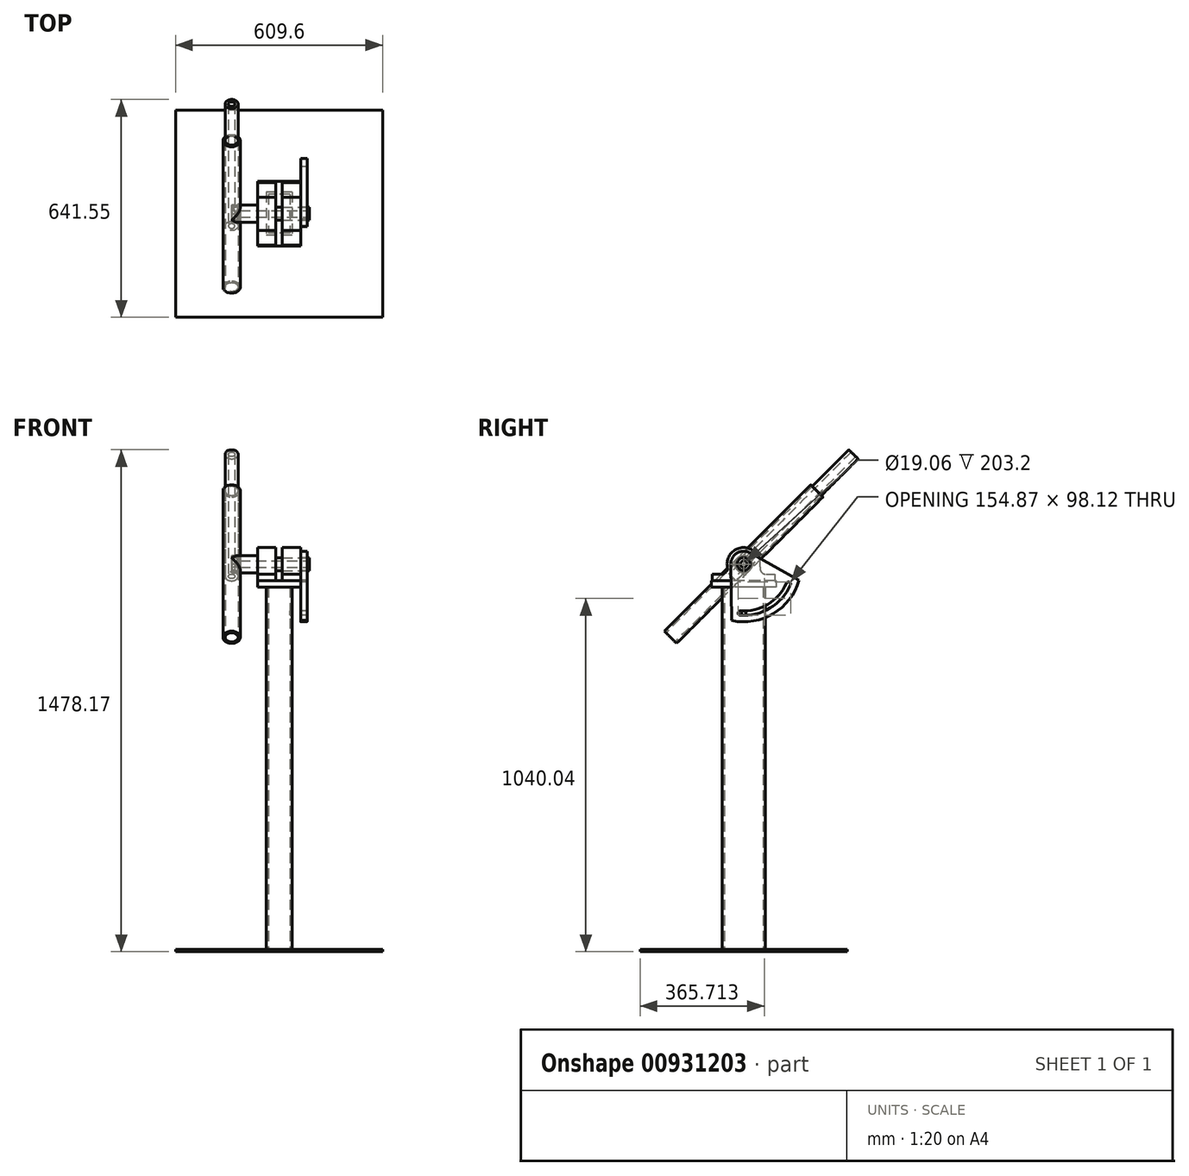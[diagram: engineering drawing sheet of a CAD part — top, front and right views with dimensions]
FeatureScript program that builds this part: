
annotation { "Feature Type Name" : "Feature", "Feature Type Description" : "" }
export const myFeature = defineFeature(function(context is Context, id is Id, definition is map)
    precondition{}
    {
        {
            var Q0;
            Q0=qCreatedBy(makeId("Top.planeOp"),FACE);
            var sketch = newSketch(context, id + "F0", { "sketchPlane" : qUnion([Q0])});
            skLineSegment(sketch, "E0.bottom", {"start": v(304.8, 304.8) * mm, "end": v(-304.8, 304.8) * mm});
            skLineSegment(sketch, "E0.top", {"start": v(304.8, -304.8) * mm, "end": v(-304.8, -304.8) * mm});
            skLineSegment(sketch, "E0.left", {"start": v(304.8, 304.8) * mm, "end": v(304.8, -304.8) * mm});
            skLineSegment(sketch, "E0.right", {"start": v(-304.8, 304.8) * mm, "end": v(-304.8, -304.8) * mm});
            skPoint(sketch, "E0.middle", {"position": v(0, 0) * mm});
            skSolve(sketch);
        }
        {
            var Q0;
            Q0 = qSketchRegion(id + "F0", true);
            extrude(context, id + "F1", {"entities" : qUnion([Q0]), "depth" : 6.35 * mm, "offsetDistance" : 25.4 * mm});
        }
        {
            var Q0;
            Q0=makeQuery(id+"F1.opExtrude","CAP_FACE",FACE,{"disambiguationData":[OSD([sQuery(id+"F0.wireOp",EDGE,"E0.bottom"),sQuery(id+"F0.wireOp",EDGE,"E0.top"),sQuery(id+"F0.wireOp",EDGE,"E0.left"),sQuery(id+"F0.wireOp",EDGE,"E0.right")])],"isStart":false});
            var sketch = newSketch(context, id + "F2", { "sketchPlane" : qUnion([Q0])});
            skLineSegment(sketch, "E1.bottom", {"start": v(38.1, 63.5) * mm, "end": v(-38.1, 63.5) * mm});
            skLineSegment(sketch, "E1.top", {"start": v(38.1, -63.5) * mm, "end": v(-38.1, -63.5) * mm});
            skLineSegment(sketch, "E1.left", {"start": v(38.1, 63.5) * mm, "end": v(38.1, -63.5) * mm});
            skLineSegment(sketch, "E1.right", {"start": v(-38.1, 63.5) * mm, "end": v(-38.1, -63.5) * mm});
            skPoint(sketch, "E1.middle", {"position": v(0, 0) * mm});
            skLineSegment(sketch, "E2.bottom", {"start": v(31.75, 57.15) * mm, "end": v(-31.75, 57.15) * mm});
            skLineSegment(sketch, "E2.top", {"start": v(31.75, -57.15) * mm, "end": v(-31.75, -57.15) * mm});
            skLineSegment(sketch, "E2.left", {"start": v(31.75, 57.15) * mm, "end": v(31.75, -57.15) * mm});
            skLineSegment(sketch, "E2.right", {"start": v(-31.75, 57.15) * mm, "end": v(-31.75, -57.15) * mm});
            skSolve(sketch);
        }
        {
            var Q0;
            Q0 = qSketchRegion(id + "F2", true);
            extrude(context, id + "F3", {"entities" : qUnion([Q0]), "depth" : 1066.8 * mm, "offsetDistance" : 25.4 * mm});
        }
        {
            var Q0;
            Q0=makeQuery(id+"F3.opExtrude","CAP_FACE",FACE,{"disambiguationData":[OSD([sQuery(id+"F2.wireOp",EDGE,"E1.bottom"),sQuery(id+"F2.wireOp",EDGE,"E1.top"),sQuery(id+"F2.wireOp",EDGE,"E1.left"),sQuery(id+"F2.wireOp",EDGE,"E1.right"),sQuery(id+"F2.wireOp",EDGE,"E2.bottom"),sQuery(id+"F2.wireOp",EDGE,"E2.top"),sQuery(id+"F2.wireOp",EDGE,"E2.left"),sQuery(id+"F2.wireOp",EDGE,"E2.right")])],"isStart":false});
            var sketch = newSketch(context, id + "F4", { "sketchPlane" : qUnion([Q0])});
            skLineSegment(sketch, "E3", {"start": v(-38.1, -63.5) * mm, "end": v(38.1, 63.5) * mm, "construction": true});
            skLineSegment(sketch, "E4.bottom", {"start": v(-63.5, 95.25) * mm, "end": v(63.5, 95.25) * mm});
            skLineSegment(sketch, "E4.top", {"start": v(-63.5, -95.25) * mm, "end": v(63.5, -95.25) * mm});
            skLineSegment(sketch, "E4.left", {"start": v(-63.5, 95.25) * mm, "end": v(-63.5, -95.25) * mm});
            skLineSegment(sketch, "E4.right", {"start": v(63.5, 95.25) * mm, "end": v(63.5, -95.25) * mm});
            skPoint(sketch, "E4.middle", {"position": v(0, 0) * mm});
            skSolve(sketch);
        }
        {
            var Q0;
            Q0 = qSketchRegion(id + "F4", true);
            extrude(context, id + "F5", {"entities" : qUnion([Q0]), "depth" : 19.05 * mm, "offsetDistance" : 25.4 * mm});
        }
        {
            var Q0;
            Q0=makeQuery(id+"F5.opExtrude","SWEPT_FACE",FACE,{"disambiguationData":[OSD([sQuery(id+"F4.wireOp",EDGE,"E4.left")])]});
            var sketch = newSketch(context, id + "F6", { "sketchPlane" : qUnion([Q0])});
            skCircle(sketch, "E5", {"center": v(0, 1141.4) * mm, "radius": 19.05 * mm});
            skArc(sketch, "E6", {"start": v(48.1, 1133.18) * mm, "mid": v(0, 1190.2) * mm, "end": v(-48.1, 1133.18) * mm});
            skLineSegment(sketch, "E7.bottom", {"start": v(92, 1111.25) * mm, "end": v(66.6, 1111.25) * mm});
            skLineSegment(sketch, "E7.top", {"start": v(92, 1092.2) * mm, "end": v(-92, 1092.2) * mm});
            skLineSegment(sketch, "E7.left", {"start": v(92, 1111.25) * mm, "end": v(92, 1092.2) * mm});
            skLineSegment(sketch, "E7.right", {"start": v(-92, 1111.25) * mm, "end": v(-92, 1092.2) * mm});
            skLineSegment(sketch, "E8", {"start": v(0, 1141.4) * mm, "end": v(0, 1092.2) * mm, "construction": true});
            skArc(sketch, "E9", {"start": v(48.1, 1133.18) * mm, "mid": v(52.26, 1117.92) * mm, "end": v(66.6, 1111.25) * mm});
            skArc(sketch, "E10", {"start": v(-66.6, 1111.25) * mm, "mid": v(-52.26, 1117.92) * mm, "end": v(-48.1, 1133.18) * mm});
            skPoint(sketch, "E11.0", {"position": v(0, 1092.2) * mm});
            skLineSegment(sketch, "E12.trimOffspring", {"start": v(-66.6, 1111.25) * mm, "end": v(-92, 1111.25) * mm});
            skSolve(sketch);
        }
        {
            var Q0;
            Q0 = qSketchRegion(id + "F6", true);
            extrude(context, id + "F7", {"entities" : qUnion([Q0]), "oppositeDirection" : true, "depth" : 54 * mm, "offsetDistance" : 25.4 * mm});
        }
        {
            var Q0;
            Q0=makeQuery(id+"F5.opExtrude","SWEPT_FACE",FACE,{"disambiguationData":[OSD([sQuery(id+"F4.wireOp",EDGE,"E4.right")])]});
            var sketch = newSketch(context, id + "F8", { "sketchPlane" : qUnion([Q0])});
            skLineSegment(sketch, "E13.0", {"start": v(-92, 1111.25) * mm, "end": v(-92, 1092.2) * mm});
            skLineSegment(sketch, "E14.0", {"start": v(-92, 1111.25) * mm, "end": v(-66.6, 1111.25) * mm});
            skLineSegment(sketch, "E15.0", {"start": v(-92, 1092.2) * mm, "end": v(92, 1092.2) * mm});
            skArc(sketch, "E16.0", {"start": v(-48.1, 1133.18) * mm, "mid": v(-52.26, 1117.92) * mm, "end": v(-66.6, 1111.25) * mm});
            skArc(sketch, "E17.0", {"start": v(-48.1, 1133.18) * mm, "mid": v(0, 1190.2) * mm, "end": v(48.1, 1133.18) * mm});
            skCircle(sketch, "E18.0", {"center": v(0, 1141.4) * mm, "radius": 19.05 * mm});
            skArc(sketch, "E19.0", {"start": v(66.6, 1111.25) * mm, "mid": v(52.26, 1117.92) * mm, "end": v(48.1, 1133.18) * mm});
            skLineSegment(sketch, "E20.0", {"start": v(66.6, 1111.25) * mm, "end": v(92, 1111.25) * mm});
            skLineSegment(sketch, "E21.0", {"start": v(92, 1111.25) * mm, "end": v(92, 1092.2) * mm});
            skSolve(sketch);
        }
        {
            var Q0;
            Q0 = qSketchRegion(id + "F8", true);
            extrude(context, id + "F9", {"entities" : qUnion([Q0]), "oppositeDirection" : true, "depth" : 54 * mm, "offsetDistance" : 25.4 * mm});
        }
        {
            var Q0;
            Q0=makeQuery(id+"F6.imprint","IMPRINT",FACE,{"disambiguationData":[TD([[makeQuery(id+"F6.imprint","IMPRINT",EDGE,{"derivedFrom":sQuery(id+"F6.wireOp",EDGE,"E5")}),-1.0]])]});
            var sketch = newSketch(context, id + "F10", { "sketchPlane" : qUnion([Q0])});
            skCircle(sketch, "E22", {"center": v(0, 1141.4) * mm, "radius": 9.53 * mm});
            skCircle(sketch, "E23", {"center": v(0, 1141.4) * mm, "radius": 19.05 * mm});
            skCircle(sketch, "E24.0", {"center": v(0, 1141.4) * mm, "radius": 19.05 * mm, "construction": true});
            skSolve(sketch);
        }
        {
            var Q0;
            Q0 = qSketchRegion(id + "F10", true);
            extrude(context, id + "F11", {"entities" : qUnion([Q0]), "depth" : 50.8 * mm, "offsetDistance" : 25.4 * mm, "hasSecondDirection" : true, "secondDirectionOppositeDirection" : true, "secondDirectionDepth" : 152.4 * mm});
        }
        {
            var Q0;
            Q0=makeQuery(id+"F3.opExtrude","SWEPT_FACE",FACE,{"disambiguationData":[OSD([sQuery(id+"F2.wireOp",EDGE,"E1.left")])]});
            var sketch = newSketch(context, id + "F12", { "sketchPlane" : qUnion([Q0])});
            skCircle(sketch, "E25", {"center": v(0, 996.95) * mm, "radius": 6.35 * mm});
            skSolve(sketch);
        }
        {
            var Q0;
            Q0 = qSketchRegion(id + "F12", true);
            extrude(context, id + "F13", {"entities" : qUnion([Q0]), "operationType" : NewBodyOperationType.REMOVE, "oppositeDirection" : true, "depth" : 25.4 * mm, "offsetDistance" : 25.4 * mm});
        }
        {
            var Q0;
            Q0=makeQuery(id+"F9.opExtrude","CAP_FACE",FACE,{"disambiguationData":[OSD([sQuery(id+"F8.wireOp",EDGE,"E13.0"),sQuery(id+"F8.wireOp",EDGE,"E14.0"),sQuery(id+"F8.wireOp",EDGE,"E15.0"),sQuery(id+"F8.wireOp",EDGE,"E16.0"),sQuery(id+"F8.wireOp",EDGE,"E17.0"),sQuery(id+"F8.wireOp",EDGE,"E18.0"),sQuery(id+"F8.wireOp",EDGE,"E19.0"),sQuery(id+"F8.wireOp",EDGE,"E20.0"),sQuery(id+"F8.wireOp",EDGE,"E21.0")])],"isStart":true});
            var sketch = newSketch(context, id + "F14", { "sketchPlane" : qUnion([Q0])});
            skLineSegment(sketch, "E26", {"start": v(-38.1, 1140.74) * mm, "end": v(-35.2, 975.24) * mm});
            skLineSegment(sketch, "E27", {"start": v(163.24, 1094.48) * mm, "end": v(18.47, 1174.72) * mm});
            skArc(sketch, "E28", {"start": v(18.47, 1174.72) * mm, "mid": v(-19.62, 1174.06) * mm, "end": v(-38.1, 1140.74) * mm});
            skArc(sketch, "E29", {"start": v(-35.2, 975.24) * mm, "mid": v(87.48, 995.81) * mm, "end": v(163.24, 1094.48) * mm});
            skCircle(sketch, "E30", {"center": v(0, 1141.4) * mm, "radius": 144.45 * mm, "construction": true});
            skCircle(sketch, "E31.0", {"center": v(0, 996.95) * mm, "radius": 6.35 * mm, "construction": true});
            skArc(sketch, "E32", {"start": v(-9.74, 1003.64) * mm, "mid": v(-16.52, 997.76) * mm, "end": v(-10.63, 990.98) * mm});
            skArc(sketch, "E33", {"start": v(137.8, 1080.17) * mm, "mid": v(134.58, 1088.55) * mm, "end": v(126.2, 1085.33) * mm});
            skArc(sketch, "E34", {"start": v(-9.74, 1003.64) * mm, "mid": v(71.13, 1023.03) * mm, "end": v(126.2, 1085.33) * mm});
            skArc(sketch, "E35", {"start": v(-10.63, 990.98) * mm, "mid": v(77.67, 1012.14) * mm, "end": v(137.8, 1080.17) * mm});
            skCircle(sketch, "E36", {"center": v(0, 1141.4) * mm, "radius": 19.05 * mm});
            skCircle(sketch, "E37.0", {"center": v(0, 1141.4) * mm, "radius": 19.05 * mm, "construction": true});
            skSolve(sketch);
        }
        {
            var Q0;
            Q0 = qSketchRegion(id + "F14", true);
            extrude(context, id + "F15", {"entities" : qUnion([Q0]), "depth" : 19.05 * mm, "offsetDistance" : 25.4 * mm});
        }
        {
            var Q0;
            Q0=sQuery(id+"F6.wireOp",VERTEX,"E8.start");
            var Q1;
            Q1=sQuery(id+"F14.wireOp",VERTEX,"E28.center");
            var Q2;
            Q2=sQuery(id+"F14.wireOp",VERTEX,"E31.0.center");
            cPlane(context, id + "F16", {"entities" : qUnion([Q0, Q1, Q2]), "cplaneType" : CPlaneType.THREE_POINT, "offset" : 25.4 * mm, "width" : 152.4 * mm, "height" : 152.4 * mm});
        }
        {
            var Q0;
            Q0=qCreatedBy(id+"F16.planeOp",FACE);
            var sketch = newSketch(context, id + "F17", { "sketchPlane" : qUnion([Q0])});
            skLineSegment(sketch, "E38.0", {"start": v(63.5, 1160.45) * mm, "end": v(63.5, 1122.35) * mm, "construction": true});
            skLineSegment(sketch, "E39", {"start": v(82.55, 1141.4) * mm, "end": v(63.5, 1141.4) * mm, "construction": true});
            skLineSegment(sketch, "E40.0", {"start": v(82.55, 1122.35) * mm, "end": v(82.55, 1160.45) * mm, "construction": true});
            skSolve(sketch);
        }
        {
            var Q0;
            Q0=sQuery(id+"F17.wireOp",EDGE,"E39");
            cPlane(context, id + "F18", {"entities" : qUnion([Q0]), "cplaneType" : CPlaneType.LINE_ANGLE, "offset" : 25.4 * mm, "angle" : 45 * degree, "oppositeDirection" : true, "width" : 152.4 * mm, "height" : 152.4 * mm});
        }
        {
            var Q0;
            Q0=makeQuery(id+"F11.opExtrude","CAP_FACE",FACE,{"disambiguationData":[OSD([sQuery(id+"F10.wireOp",EDGE,"E22"),sQuery(id+"F10.wireOp",EDGE,"E23")])],"isStart":false});
            var sketch = newSketch(context, id + "F19", { "sketchPlane" : qUnion([Q0])});
            skCircle(sketch, "E41.0", {"center": v(0, 1141.4) * mm, "radius": 19.05 * mm});
            skCircle(sketch, "E42", {"center": v(0, 1141.4) * mm, "radius": 25.4 * mm});
            skSolve(sketch);
        }
        {
            var Q0;
            Q0 = qSketchRegion(id + "F19", true);
            extrude(context, id + "F20", {"entities" : qUnion([Q0]), "oppositeDirection" : true, "depth" : 50.8 * mm, "offsetDistance" : 25.4 * mm, "hasSecondDirection" : true, "secondDirectionOppositeDirection" : false, "secondDirectionDepth" : 25.4 * mm});
        }
        {
            var Q0;
            Q0=qCreatedBy(id+"F18.planeOp",FACE);
            var sketch = newSketch(context, id + "F21", { "sketchPlane" : qUnion([Q0])});
            skLineSegment(sketch, "E43.0", {"start": v(-114.3, 788.04) * mm, "end": v(-114.3, 826.14) * mm, "construction": true});
            skLineSegment(sketch, "E44.0", {"start": v(-139.7, 788.04) * mm, "end": v(-139.7, 826.14) * mm, "construction": true});
            skLineSegment(sketch, "E45.0", {"start": v(-139.7, 781.7) * mm, "end": v(-139.7, 832.5) * mm, "construction": true});
            skCircle(sketch, "E46", {"center": v(-139.7, 807.1) * mm, "radius": 25.4 * mm});
            skCircle(sketch, "E47", {"center": v(-139.7, 807.1) * mm, "radius": 19.05 * mm});
            skSolve(sketch);
        }
        {
            var Q0;
            Q0 = qSketchRegion(id + "F21", true);
            extrude(context, id + "F22", {"entities" : qUnion([Q0]), "oppositeDirection" : true, "depth" : 304.8 * mm, "offsetDistance" : 25.4 * mm, "hasSecondDirection" : true, "secondDirectionOppositeDirection" : false, "secondDirectionDepth" : 304.8 * mm});
        }
        {
            var Q0;
            Q0=makeQuery(id+"F22.opExtrude","SWEPT_BODY",BODY,{"disambiguationData":[OSD([sQuery(id+"F21.wireOp",EDGE,"E46"),sQuery(id+"F21.wireOp",EDGE,"E47")])]});
            var Q1;
            Q1=makeQuery(id+"F20.opExtrude","SWEPT_BODY",BODY,{"disambiguationData":[OSD([sQuery(id+"F19.wireOp",EDGE,"E41.0"),sQuery(id+"F19.wireOp",EDGE,"E42")])]});
            booleanBodies(context, id + "F23", {"operationType" : BooleanOperationType.SUBTRACTION, "tools" : qUnion([Q0]), "targets" : qUnion([Q1]), "keepTools" : true});
        }
        {
            var Q0;
            Q0=makeQuery(id+"F22.opExtrude","SWEPT_BODY",BODY,{"disambiguationData":[OSD([sQuery(id+"F21.wireOp",EDGE,"E46"),sQuery(id+"F21.wireOp",EDGE,"E47")])]});
            var Q1;
            Q1=makeQuery(id+"F23.opBoolean","SPLIT",BODY,{"disambiguationData":[OD(0.0)],"derivedFrom":makeQuery(id+"F20.opExtrude","SWEPT_BODY",BODY,{"disambiguationData":[OSD([sQuery(id+"F19.wireOp",EDGE,"E41.0"),sQuery(id+"F19.wireOp",EDGE,"E42")])]})});
            booleanBodies(context, id + "F24", {"operationType" : BooleanOperationType.UNION, "tools" : qUnion([Q0, Q1])});
        }
        {
            var Q0;
            Q0=makeQuery(id+"F22.opExtrude","CAP_FACE",FACE,{"disambiguationData":[OSD([sQuery(id+"F21.wireOp",EDGE,"E46"),sQuery(id+"F21.wireOp",EDGE,"E47")])],"isStart":false});
            var sketch = newSketch(context, id + "F25", { "sketchPlane" : qUnion([Q0])});
            skCircle(sketch, "E48.0", {"center": v(139.7, 807.1) * mm, "radius": 25.4 * mm, "construction": true});
            skCircle(sketch, "E49", {"center": v(139.7, 807.1) * mm, "radius": 19.05 * mm});
            skCircle(sketch, "E50", {"center": v(139.7, 807.1) * mm, "radius": 9.53 * mm});
            skSolve(sketch);
        }
        {
            var Q0;
            Q0 = qSketchRegion(id + "F25", true);
            extrude(context, id + "F26", {"entities" : qUnion([Q0]), "depth" : 152.4 * mm, "offsetDistance" : 25.4 * mm, "hasSecondDirection" : true, "secondDirectionOppositeDirection" : true, "secondDirectionDepth" : 355.6 * mm});
        }
        {
            var Q0;
            Q0 = qSketchRegion(id + "F6", true);
            extrude(context, id + "F27", {"entities" : qUnion([Q0]), "operationType" : NewBodyOperationType.ADD, "oppositeDirection" : true, "depth" : 54 * mm, "offsetDistance" : 25.4 * mm});
        }
    });
